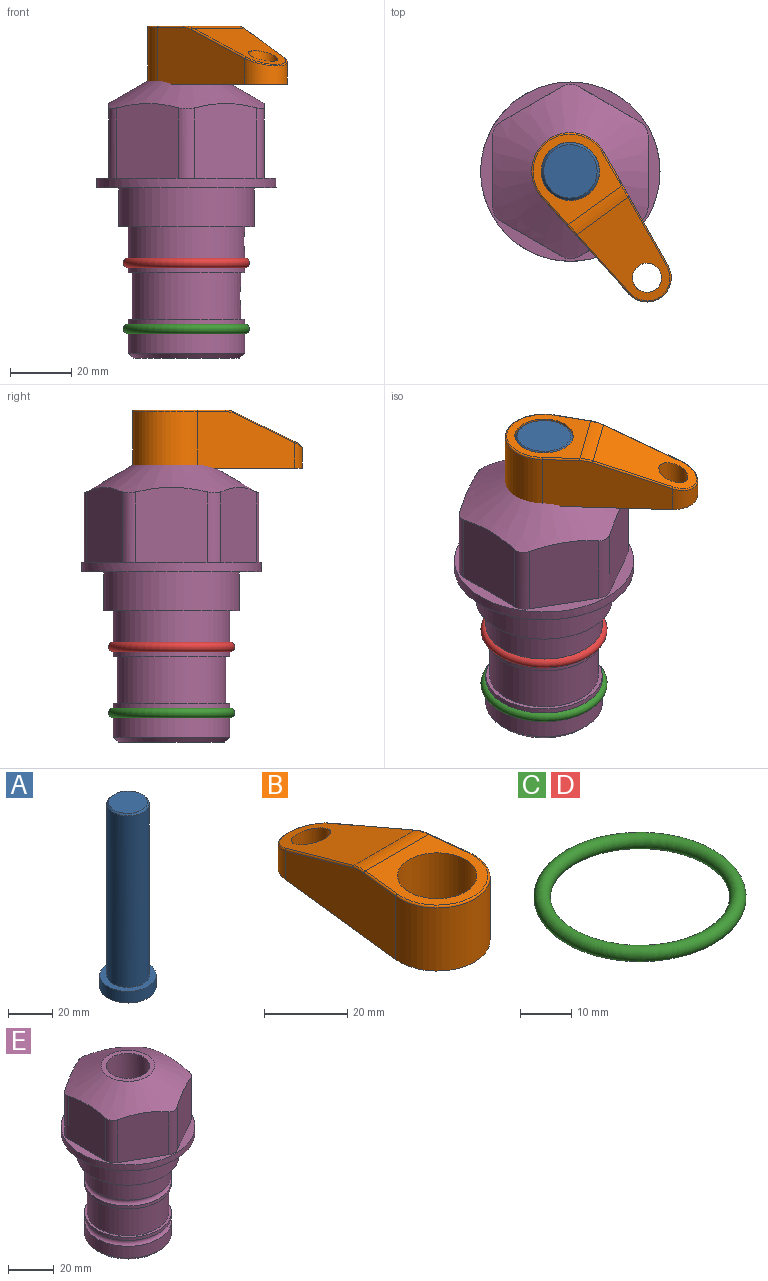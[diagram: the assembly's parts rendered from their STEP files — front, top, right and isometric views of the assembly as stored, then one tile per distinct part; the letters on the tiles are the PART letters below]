
ASSEMBLY  parts=5 mates=3
PART A: 6 faces, bbox 25.4x25.4x101.6 mm
  f0: plane 17.46x17.46mm, normal (0,0,1), area 239.5mm2, adj f5
  f1: plane 25.4x25.4mm, normal (0,0,-1), area 506.7mm2, adj f2
  f2: cylinder r=12.7mm len=25.4mm, axis (0,0,1), area 506.7mm2, adj f1,f3
  f3: plane 25.4x25.4mm, normal (0,0,1), area 221.7mm2, adj f2,f4
  f4: cylinder r=9.53mm len=94.46mm, axis (0,0,1), area 5653mm2, adj f3,f5
  f5: cone r=8.73mm half-angle=45deg, axis (0,0,-1), area 64.4mm2, adj f0,f4
PART B: 44 faces, bbox 27.5x64.5x19.1 mm
  f0: plane 2.3x0.95mm, normal (0,0,-1), area 1mm2, adj f25,f30,f34
  f1: plane 63.5x25.4mm, normal (0,0,-1), area 561.7mm2, adj f2,f3,f4,f5,f6,f7,f19,f20
  f2: cylinder r=12.7mm len=25.4mm, axis (0,0,-1), area 792.2mm2, adj f1,f3,f5,f13
  f3: plane 42.33x18.54mm, normal (0.99,0.11,0), area 647mm2, adj f1,f2,f4,f11,f12,f14
  f4: cylinder r=7.94mm len=15.78mm, axis (0,0,-1), area 158.6mm2, adj f1,f3,f5,f16
  f5: plane 42.33x18.54mm, normal (-0.99,0.11,0), area 647mm2, adj f1,f2,f4,f15,f17,f18
  f6: cylinder r=9.53mm len=19.05mm, axis (0,0,-1), area 1140.1mm2, adj f1,f8
  f7: cylinder r=4.76mm len=10.98mm, axis (0,0,-1), area 276.1mm2, adj f1,f9
  f8: plane 25.83x24.38mm, normal (0,0,1), area 262.2mm2, adj f6,f10,f11,f13,f15
  f9: plane 32.49x20.55mm, normal (0,0.34,0.94), area 489.9mm2, adj f7,f10,f14,f16,f18
  f10: cylinder r=12.7mm len=21.49mm, axis (-1,0,0), area 93.2mm2, adj f8,f9,f12,f17
  f11: cylinder r=0.51mm len=12.34mm, axis (0.11,-0.99,0), area 9.9mm2, adj f3,f8,f12,f13
  f12: bspline ~7.62x1.64mm, area 3.5mm2, adj f3,f10,f11,f14
  f13: torus R=12.19mm, axis (0,0,1), area 33.6mm2, adj f2,f8,f11,f15
  f14: cylinder r=0.51mm len=26.01mm, axis (0.1,-0.93,0.34), area 21.6mm2, adj f3,f9,f12,f16
  f15: cylinder r=0.51mm len=12.34mm, axis (0.11,0.99,0), area 9.9mm2, adj f5,f8,f13,f17
  f16: bspline ~15.78x7.05mm, area 15.7mm2, adj f4,f9,f14,f18
  f17: bspline ~7.62x1.64mm, area 3.5mm2, adj f5,f10,f15,f18
  f18: cylinder r=0.51mm len=26.01mm, axis (0.1,0.93,-0.34), area 21.6mm2, adj f5,f9,f16,f17
  f19: plane 21.6x14.29mm, normal (-0.99,-0.11,0), area 242.6mm2, adj f1,f26,f28,f34,f36,f38
  f20: plane 21.6x14.29mm, normal (0.99,-0.11,0), area 242.6mm2, adj f1,f27,f29,f37,f39,f41
  f21: cylinder r=12.7mm len=14.29mm, axis (0,0,-1), area 173.2mm2, adj f1,f26,f27,f30,f31,f33
  f22: cylinder r=7.94mm len=7.63mm, axis (0,0,-1), area 53.8mm2, adj f1,f28,f29,f42
  f23: plane 2.3x0.95mm, normal (0,0,-1), area 1mm2, adj f25,f33,f37
  f24: plane 17.94x12.32mm, normal (0,-0.34,-0.94), area 191.2mm2, adj f25,f38,f41,f42
  f25: cylinder r=9.53mm len=12.93mm, axis (-1,0,0), area 37.5mm2, adj f0,f23,f24,f31,f36,f39
  f26: cylinder r=1.59mm len=14.29mm, axis (0,0,-1), area 49mm2, adj f1,f19,f21,f32
  f27: cylinder r=1.59mm len=14.29mm, axis (0,0,-1), area 49mm2, adj f1,f20,f21,f35
  f28: cylinder r=1.59mm len=7.28mm, axis (0,0,-1), area 22.1mm2, adj f1,f19,f22,f40
  f29: cylinder r=1.59mm len=7.28mm, axis (0,0,-1), area 22.1mm2, adj f1,f20,f22,f43
  f30: torus R=14.29mm, axis (0,0,1), area 5.8mm2, adj f0,f21,f31,f32
  f31: bspline ~11.06x2.73mm, area 20.8mm2, adj f21,f25,f30,f33
  f32: sphere r=1.59mm, area 5.4mm2, adj f26,f30,f34
  f33: torus R=14.29mm, axis (0,0,1), area 5.8mm2, adj f21,f23,f31,f35
  f34: cylinder r=1.59mm len=1.68mm, axis (-0.11,0.99,0), area 2.4mm2, adj f0,f19,f32,f36
  f35: sphere r=1.59mm, area 5.4mm2, adj f27,f33,f37
  f36: bspline ~5.82x2.33mm, area 7.7mm2, adj f19,f25,f34,f38
  f37: cylinder r=1.59mm len=1.68mm, axis (0.11,0.99,0), area 2.4mm2, adj f20,f23,f35,f39
  f38: cylinder r=1.59mm len=18.33mm, axis (0.1,-0.93,0.34), area 46.7mm2, adj f19,f24,f36,f40
  f39: bspline ~5.82x2.33mm, area 7.7mm2, adj f20,f25,f37,f41
  f40: sphere r=1.59mm, area 3.6mm2, adj f28,f38,f42
  f41: cylinder r=1.59mm len=18.33mm, axis (0.1,0.93,-0.34), area 46.7mm2, adj f20,f24,f39,f43
  f42: bspline ~8.31x1.84mm, area 15.3mm2, adj f22,f24,f40,f43
  f43: sphere r=1.59mm, area 3.6mm2, adj f29,f41,f42
PART C: 1 faces, bbox 44.7x44.7x3.2 mm
  f0: torus R=19.05mm, axis (0,0,1), area 1193.9mm2
PART D: same geometry as C
PART E: 36 faces, bbox 58.7x58.7x91.2 mm
  f0: cylinder r=17.78mm len=35.56mm, axis (0,0,1), area 1670.8mm2, adj f23,f24,f31
  f1: cylinder r=19.05mm len=38.1mm, axis (0,0,1), area 1191.9mm2, adj f26,f27,f30
  f2: plane 58.66x58.66mm, normal (0,0,-1), area 1150.6mm2, adj f3,f28
  f3: cylinder r=29.33mm len=58.66mm, axis (0,0,-1), area 585.1mm2, adj f2,f4
  f4: plane 58.66x58.66mm, normal (0,0,1), area 475.9mm2, adj f3,f5,f6,f7,f8,f9,f10,f11
  f5: plane 24.5x20.32mm, normal (-0.5,0.87,0), area 562.8mm2, adj f4,f15,f16,f17
  f6: plane 24.5x20.32mm, normal (0.5,0.87,0), area 562.8mm2, adj f4,f14,f15,f17
  f7: plane 24.5x23.48mm, normal (1,0,0), area 562.8mm2, adj f4,f13,f14,f17
  f8: plane 24.5x20.32mm, normal (0.5,-0.87,0), area 562.8mm2, adj f4,f12,f13,f17
  f9: plane 24.5x20.32mm, normal (-0.5,-0.87,0), area 562.8mm2, adj f4,f11,f12,f17
  f10: plane 24.5x23.48mm, normal (-1,0,0), area 562.8mm2, adj f4,f11,f16,f17
  f11: cylinder r=5.08mm len=23.01mm, axis (0,0,-1), area 121.2mm2, adj f4,f9,f10,f17
  f12: cylinder r=5.08mm len=23.01mm, axis (0,0,-1), area 121.2mm2, adj f4,f8,f9,f17
  f13: cylinder r=5.08mm len=23.01mm, axis (0,0,-1), area 121.2mm2, adj f4,f7,f8,f17
  f14: cylinder r=5.08mm len=23.01mm, axis (0,0,-1), area 121.2mm2, adj f4,f6,f7,f17
  f15: cylinder r=5.08mm len=23.01mm, axis (0,0,-1), area 121.2mm2, adj f4,f5,f6,f17
  f16: cylinder r=5.08mm len=23.01mm, axis (0,0,-1), area 121.2mm2, adj f4,f5,f10,f17
  f17: cone r=11.73mm half-angle=60deg, axis (0,0,-1), area 2071.8mm2, adj f5,f6,f7,f8,f9,f10,f11,f12
  f18: plane 23.46x23.46mm, normal (0,0,1), area 147.4mm2, adj f17,f35
  f19: plane 34.93x34.93mm, normal (0,0,-1), area 958mm2, adj f29
  f20: cylinder r=19.05mm len=38.1mm, axis (0,0,1), area 760.1mm2, adj f21,f29
  f21: torus R=19.05mm, axis (0,0,1), area 565.3mm2, adj f20,f22
  f22: cylinder r=19.05mm len=38.1mm, axis (0,0,1), area 190mm2, adj f21,f23
  f23: plane 38.1x38.1mm, normal (0,0,1), area 146.9mm2, adj f0,f22
  f24: plane 38.1x38.1mm, normal (0,0,-1), area 146.9mm2, adj f0,f25
  f25: cylinder r=19.05mm len=38.1mm, axis (0,0,1), area 190mm2, adj f24,f26
  f26: torus R=19.05mm, axis (0,0,1), area 565.3mm2, adj f1,f25
  f27: plane 44.45x44.45mm, normal (0,0,-1), area 411.7mm2, adj f1,f28
  f28: cylinder r=22.23mm len=44.45mm, axis (0,0,1), area 1773.5mm2, adj f2,f27
  f29: cone r=19.05mm half-angle=45deg, axis (0,0,1), area 257.5mm2, adj f19,f20
  f30: cylinder r=3.17mm len=6.75mm, axis (-1,0,0), area 128mm2, adj f1,f33
  f31: cylinder r=3.17mm len=6.35mm, axis (-1,0,0), area 102.5mm2, adj f0,f33
  f32: plane 25.4x25.4mm, normal (0,0,1), area 506.7mm2, adj f33
  f33: cylinder r=12.7mm len=66.42mm, axis (0,0,-1), area 5236.2mm2, adj f30,f31,f32,f34
  f34: cone r=9.53mm half-angle=30deg, axis (0,0,-1), area 443.4mm2, adj f33,f35
  f35: cylinder r=9.53mm len=19.05mm, axis (0,0,-1), area 849mm2, adj f18,f34
PLACE A rot(axis=(0,0,-1),54.2deg) t=(0,0,-20.67)mm
PLACE B rot(axis=(0,0,-1),144.2deg) t=(0,0,33.94)mm
PLACE C t=(0,0,-21.59)mm
PLACE D at identity
PLACE E at identity fixed
MATE fastened C.f0 <-> E.f0  axis (0,0,1) through (0,0,-46.1)mm
MATE cylindrical A.f2 <-> E.f0  axis (0,0,1) through (0,0,4.97)mm
MATE fastened B.f2 <-> A.f2  axis (0,0,1) through (0,0,52.99)mm
